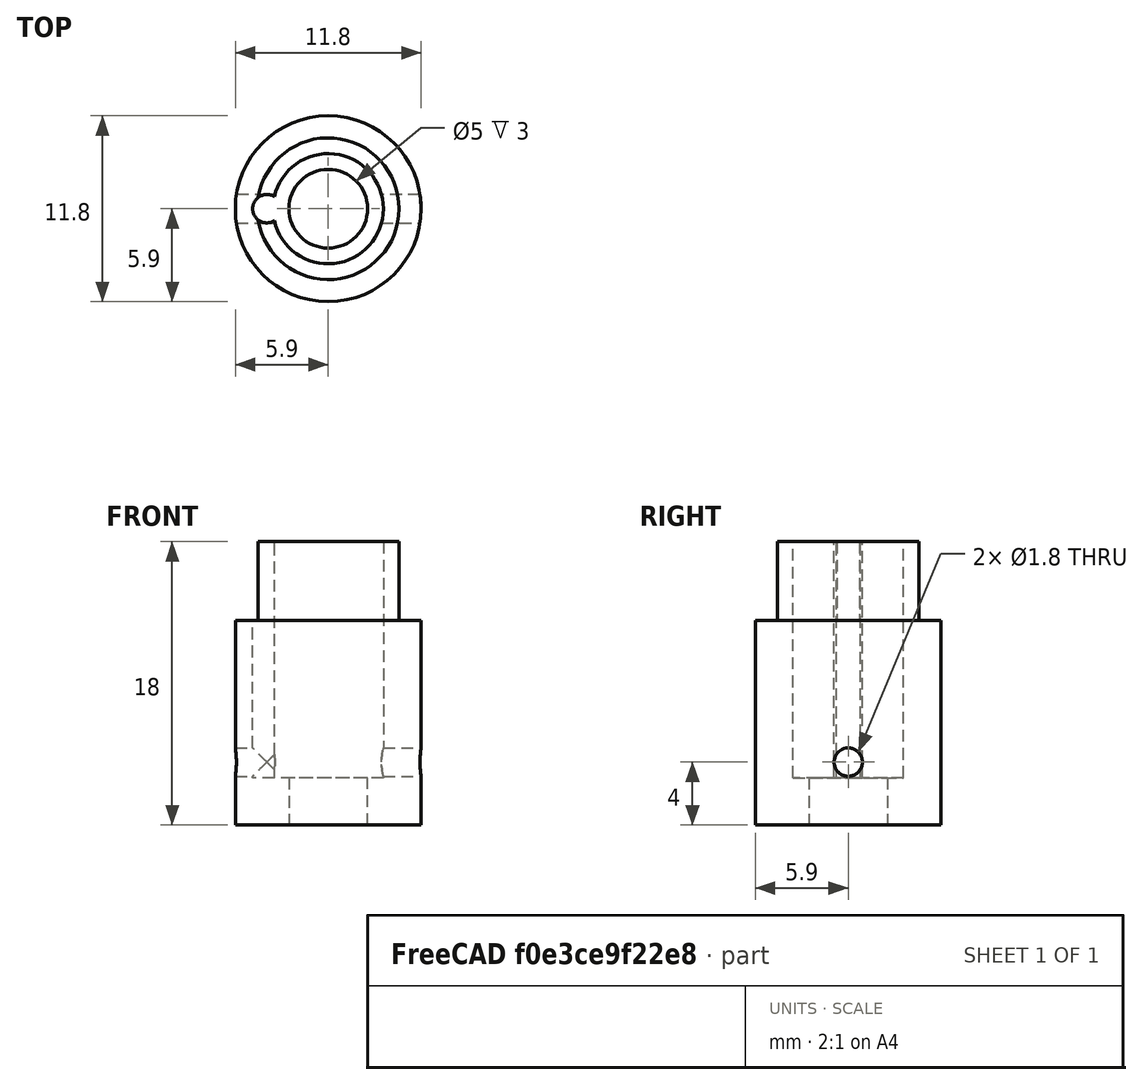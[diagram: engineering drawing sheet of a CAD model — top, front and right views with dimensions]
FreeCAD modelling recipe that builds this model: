
FCSTD DOCUMENT  (FreeCAD 0.19R24366 (Git))
Label: smoker_part
License: All rights reserved
LicenseURL: http://en.wikipedia.org/wiki/All_rights_reserved
objects: Sketcher::SketchObject×7, PartDesign::Pocket×4, PartDesign::Pad×3, PartDesign::Body×1, Mesh::Feature×1
note: 22 computed .brp shape members not serialized (recipe doc carries the construction recipe); baked Part::Feature solids carry a one-line shape summary decoded from their .brp

FEATURE [Sketcher::SketchObject] Sketch
  FullyConstrained = true
  MapMode = 5
  Support = -> [XY_Plane]
  sketch-geometry (1):
    g0: Circle CenterX=0 CenterY=0 CenterZ=0 NormalX=0 NormalY=0 NormalZ=1 AngleXU=0 Radius=5.9
  constraints (2):
    c: Radius(g0) = 5.9
    c: Coincident(g0,g-1)
FEATURE [PartDesign::Pad] Pad
  Direction = (1,1,1)
  Length = 10
  Length2 = 100
  Profile = -> Sketch
  Type = 0
FEATURE [Sketcher::SketchObject] Sketch001
  FullyConstrained = true
  MapMode = 5
  Placement = pos=(0,0,10) rot=(0,0,1;0rad)
  Support = -> [Pad]
  sketch-geometry (1):
    g0: Circle CenterX=0 CenterY=0 CenterZ=0 NormalX=0 NormalY=0 NormalZ=1 AngleXU=0 Radius=4.5
  constraints (2):
    c: Coincident(g0,g-1)
    c: Radius(g0) = 4.5
FEATURE [PartDesign::Pad] Pad001
  BaseFeature = -> Pad
  Direction = (1,1,1)
  Length = 5
  Length2 = 100
  Profile = -> Sketch001
  Type = 0
FEATURE [Sketcher::SketchObject] Sketch002
  FullyConstrained = true
  MapMode = 5
  Placement = pos=(0,0,15) rot=(0,0,1;0rad)
  Support = -> [Pad001]
  sketch-geometry (1):
    g0: Circle CenterX=0 CenterY=0 CenterZ=0 NormalX=0 NormalY=0 NormalZ=1 AngleXU=0 Radius=3.5
  constraints (2):
    c: Coincident(g0,g-1)
    c: Radius(g0) = 3.5
FEATURE [PartDesign::Pocket] Pocket
  BaseFeature = -> Pad001
  Length = 5
  Length2 = 100
  Profile = -> Sketch002
  Type = 1
FEATURE [Sketcher::SketchObject] Sketch003
  FullyConstrained = true
  MapMode = 5
  Placement = pos=(0,0,15) rot=(0,0,1;0rad)
  Support = -> [Pocket]
  sketch-geometry (1):
    g0: Circle CenterX=-3.9 CenterY=0 CenterZ=0 NormalX=0 NormalY=0 NormalZ=1 AngleXU=0 Radius=0.9
  constraints (3):
    c: PointOnObject(g0,g-1)
    c: Radius(g0) = 0.9
    c: DistanceX(g0,g-1) = 3.9
FEATURE [PartDesign::Pocket] Pocket001
  BaseFeature = -> Pocket
  Length = 15
  Length2 = 100
  Profile = -> Sketch003
  Type = 4
FEATURE [Sketcher::SketchObject] Sketch004
  FullyConstrained = true
  MapMode = 5
  Placement = pos=(0,0,0) rot=(1,0,0;3.14159rad)
  Support = -> [Pocket001]
  sketch-geometry (1):
    g0: Circle CenterX=0 CenterY=0 CenterZ=0 NormalX=0 NormalY=0 NormalZ=1 AngleXU=0 Radius=5.9
  constraints (2):
    c: Coincident(g0,g-1)
    c: Radius(g0) = 5.9
FEATURE [PartDesign::Pad] Pad002
  BaseFeature = -> Pocket001
  Direction = (1,1,1)
  Length = 3
  Length2 = 100
  Profile = -> Sketch004
  Type = 0
FEATURE [Sketcher::SketchObject] Sketch005
  FullyConstrained = true
  MapMode = 5
  Placement = pos=(0,0,-3) rot=(1,0,0;3.14159rad)
  Support = -> [Pad002]
  sketch-geometry (1):
    g0: Circle CenterX=0 CenterY=0 CenterZ=0 NormalX=0 NormalY=0 NormalZ=1 AngleXU=0 Radius=2.5
  constraints (2):
    c: Coincident(g0,g-1)
    c: Radius(g0) = 2.5
FEATURE [PartDesign::Pocket] Pocket002
  BaseFeature = -> Pad002
  Length = 3
  Length2 = 100
  Profile = -> Sketch005
  Type = 0
FEATURE [Sketcher::SketchObject] Sketch006
  FullyConstrained = true
  MapMode = 5
  Placement = pos=(0,0,0) rot=(0.57735,0.57735,0.57735;2.0944rad)
  Support = -> [YZ_Plane]
  sketch-geometry (1):
    g0: Circle CenterX=0 CenterY=1 CenterZ=0 NormalX=0 NormalY=0 NormalZ=1 AngleXU=0 Radius=0.9
  constraints (3):
    c: PointOnObject(g0,g-2)
    c: Radius(g0) = 0.9
    c: DistanceY(g-1,g0) = 1
FEATURE [PartDesign::Pocket] Pocket003
  BaseFeature = -> Pocket002
  Length = 14
  Length2 = 14
  Profile = -> Sketch006
  Type = 4
FEATURE [PartDesign::Body] Body  label="smoker_pump_joiner"
  Group = -> [Sketch,Pad,Sketch001,Pad001,Sketch002,Pocket,Sketch003,Pocket001,Sketch004,Pad002,Sketch005,Pocket002,Sketch006,Pocket003]
  Origin = -> Origin
  Tip = -> Pocket003
FEATURE [Mesh::Feature] Mesh  label="smoker_pump_joiner (Meshed)"
